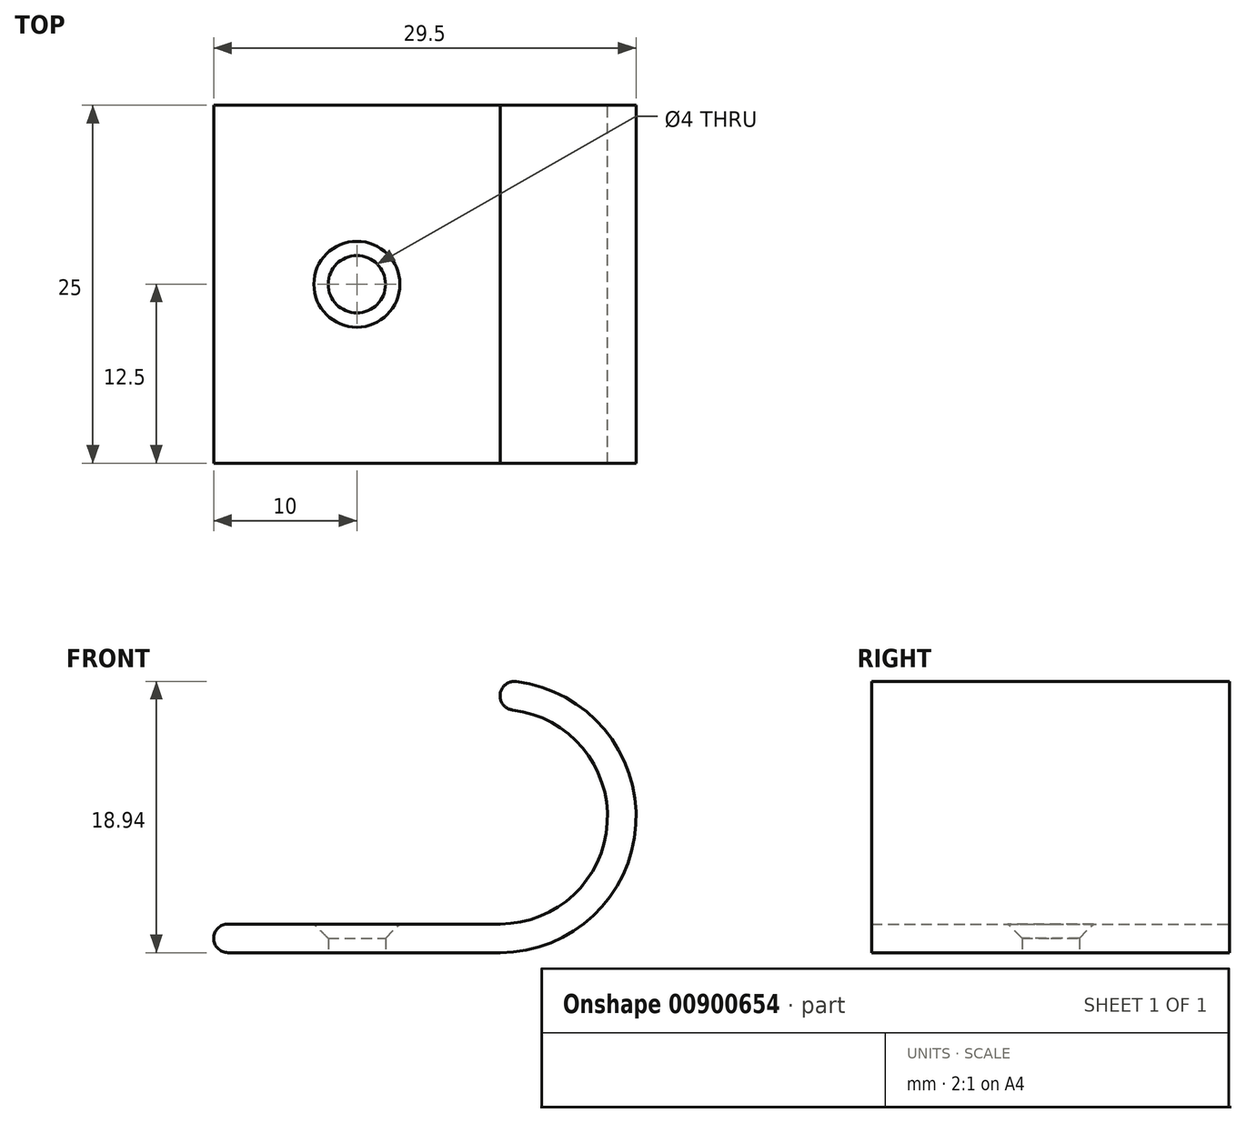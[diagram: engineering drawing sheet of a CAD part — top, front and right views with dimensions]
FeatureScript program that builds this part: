
annotation { "Feature Type Name" : "Feature", "Feature Type Description" : "" }
export const myFeature = defineFeature(function(context is Context, id is Id, definition is map)
    precondition{}
    {
        {
            var Q0;
            Q0=qCreatedBy(makeId("Front.planeOp"),FACE);
            var sketch = newSketch(context, id + "F0", { "sketchPlane" : qUnion([Q0])});
            skLineSegment(sketch, "E0.bottom", {"start": v(10, 1) * mm, "end": v(-10, 1) * mm});
            skLineSegment(sketch, "E0.top", {"start": v(10, -1) * mm, "end": v(-10, -1) * mm});
            skLineSegment(sketch, "E0.right", {"start": v(-10, 1) * mm, "end": v(-10, -1) * mm});
            skPoint(sketch, "E0.middle", {"position": v(0, 0) * mm});
            skArc(sketch, "E1", {"start": v(10, 1) * mm, "mid": v(17.5, 8.5) * mm, "end": v(10, 16) * mm});
            skArc(sketch, "E2.0", {"start": v(10, -1) * mm, "mid": v(19.5, 8.5) * mm, "end": v(10, 18) * mm});
            skLineSegment(sketch, "E3", {"start": v(10, 18) * mm, "end": v(10, 16) * mm});
            skSolve(sketch);
        }
        {
            var Q0;
            Q0=makeQuery(id+"F0.imprint","IMPRINT",FACE,{"disambiguationData":[TD([[makeQuery(id+"F0.imprint","IMPRINT",EDGE,{"derivedFrom":sQuery(id+"F0.wireOp",EDGE,"E0.bottom")}),1.0]])]});
            extrude(context, id + "F1", {"entities" : qUnion([Q0]), "endBound" : BoundingType.SYMMETRIC, "depth" : 25 * mm, "offsetDistance" : 25 * mm});
        }
        {
            var Q0;
            Q0=makeQuery(id+"F1.opExtrude","SWEPT_FACE",FACE,{"disambiguationData":[OSD([sQuery(id+"F0.wireOp",EDGE,"E0.top")])]});
            var sketch = newSketch(context, id + "F2", { "sketchPlane" : qUnion([Q0])});
            skCircle(sketch, "E4", {"center": v(0, 0) * mm, "radius": 2 * mm});
            skSolve(sketch);
        }
        {
            var Q0;
            Q0=makeQuery(id+"F2.imprint","IMPRINT",FACE,{"disambiguationData":[TD([[makeQuery(id+"F2.imprint","IMPRINT",EDGE,{"derivedFrom":sQuery(id+"F2.wireOp",EDGE,"E4")}),1.0]])]});
            extrude(context, id + "F3", {"entities" : qUnion([Q0]), "operationType" : NewBodyOperationType.REMOVE, "oppositeDirection" : true, "depth" : 25 * mm, "offsetDistance" : 25 * mm});
        }
        {
            var Q0;
            Q0=makeQuery(id+"F3.boolean.opBoolean","INTERSECT",EDGE,{"derivedFrom":[makeQuery(id+"F1.opExtrude","SWEPT_FACE",FACE,{"disambiguationData":[OSD([sQuery(id+"F0.wireOp",EDGE,"E0.bottom")])]}),makeQuery(id+"F3.opExtrude","SWEPT_FACE",FACE,{"disambiguationData":[OSD([sQuery(id+"F2.wireOp",EDGE,"E4")])]})]});
            chamfer(context, id + "F4", {"entities" : qUnion([Q0]), "width" : 1 * mm, "tangentPropagation" : true});
        }
        {
            var Q0;
            Q0=makeQuery(id+"F1.opExtrude","SWEPT_EDGE",EDGE,{"disambiguationData":[OSD([sQuery(id+"F0.wireOp",EDGE,"E2.0"),sQuery(id+"F0.wireOp",EDGE,"E3")])]});
            var Q1;
            Q1=makeQuery(id+"F1.opExtrude","SWEPT_EDGE",EDGE,{"disambiguationData":[OSD([sQuery(id+"F0.wireOp",EDGE,"E1"),sQuery(id+"F0.wireOp",EDGE,"E3")])]});
            var Q2;
            Q2=makeQuery(id+"F1.opExtrude","SWEPT_EDGE",EDGE,{"disambiguationData":[OSD([sQuery(id+"F0.wireOp",EDGE,"E0.bottom"),sQuery(id+"F0.wireOp",EDGE,"E0.right")])]});
            var Q3;
            Q3=makeQuery(id+"F1.opExtrude","SWEPT_EDGE",EDGE,{"disambiguationData":[OSD([sQuery(id+"F0.wireOp",EDGE,"E0.top"),sQuery(id+"F0.wireOp",EDGE,"E0.right")])]});
            fillet(context, id + "F5", {"entities" : qUnion([Q0, Q1, Q2, Q3]), "tangentPropagation" : true, "radius" : 1 * mm, "defaultsChanged" : false, "vertexSettings" : [], "allowEdgeOverflow" : false});
        }
    });
